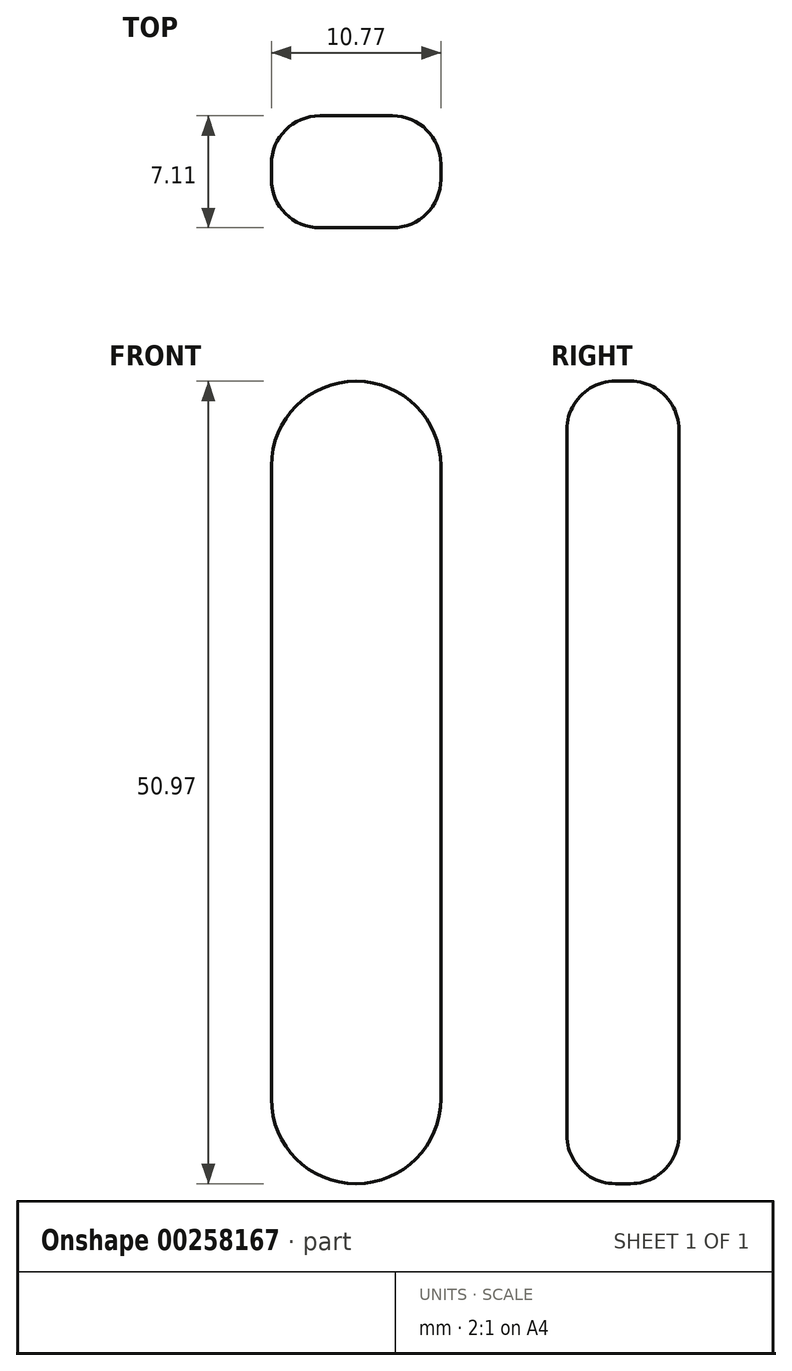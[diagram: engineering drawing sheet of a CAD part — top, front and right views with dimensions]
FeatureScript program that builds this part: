
annotation { "Feature Type Name" : "Feature", "Feature Type Description" : "" }
export const myFeature = defineFeature(function(context is Context, id is Id, definition is map)
    precondition{}
    {
        {
            var Q0;
            Q0=qCreatedBy(makeId("Front.planeOp"),FACE);
            var sketch = newSketch(context, id + "F0", { "sketchPlane" : qUnion([Q0])});
            skLineSegment(sketch, "E0", {"start": v(5.5, -31.28) * mm, "end": v(5.5, -5.4) * mm});
            skLineSegment(sketch, "E1", {"start": v(-5.26, -31.28) * mm, "end": v(-5.26, -12.39) * mm});
            skLineSegment(sketch, "E2", {"start": v(-5.26, -12.39) * mm, "end": v(-5.26, -5.4) * mm});
            skArc(sketch, "E3", {"start": v(-5.26, -5.4) * mm, "mid": v(0.12, -0.02) * mm, "end": v(5.5, -5.4) * mm});
            skArc(sketch, "E4", {"start": v(-5.26, -5.4) * mm, "mid": v(0.12, -10.79) * mm, "end": v(5.5, -5.4) * mm});
            skLineSegment(sketch, "E5", {"start": v(-5.26, -5.4) * mm, "end": v(5.5, -5.4) * mm});
            skLineSegment(sketch, "E6", {"start": v(-5.26, -5.4) * mm, "end": v(-5.26, 2.41) * mm});
            skLineSegment(sketch, "E7", {"start": v(-5.26, 2.41) * mm, "end": v(-5.26, 8.92) * mm});
            skLineSegment(sketch, "E8", {"start": v(5.5, -5.4) * mm, "end": v(5.5, 8.92) * mm});
            skLineSegment(sketch, "E9", {"start": v(5.5, 8.92) * mm, "end": v(5.5, 1.76) * mm});
            skLineSegment(sketch, "E10", {"start": v(5.5, 1.76) * mm, "end": v(5.5, 5.97) * mm});
            skArc(sketch, "E11", {"start": v(-5.26, 8.92) * mm, "mid": v(0.12, 14.3) * mm, "end": v(5.5, 8.92) * mm});
            skArc(sketch, "E12", {"start": v(5.5, -31.28) * mm, "mid": v(0.12, -36.67) * mm, "end": v(-5.26, -31.28) * mm});
            skSolve(sketch);
        }
        {
            var Q0;
            Q0=makeQuery(id+"F0.imprint","IMPRINT",FACE,{"disambiguationData":[TD([[makeQuery(id+"F0.imprint","IMPRINT",EDGE,{"derivedFrom":sQuery(id+"F0.wireOp",EDGE,"E3")}),1.0]])]});
            var Q1;
            Q1=makeQuery(id+"F0.imprint","IMPRINT",FACE,{"disambiguationData":[TD([[makeQuery(id+"F0.imprint","IMPRINT",EDGE,{"derivedFrom":sQuery(id+"F0.wireOp",EDGE,"E3")}),-1.0]])]});
            var Q2;
            Q2=makeQuery(id+"F0.imprint","IMPRINT",FACE,{"disambiguationData":[TD([[makeQuery(id+"F0.imprint","IMPRINT",EDGE,{"derivedFrom":sQuery(id+"F0.wireOp",EDGE,"E4")}),1.0]])]});
            var Q3;
            Q3=makeQuery(id+"F0.imprint","IMPRINT",FACE,{"disambiguationData":[TD([[makeQuery(id+"F0.imprint","IMPRINT",EDGE,{"derivedFrom":sQuery(id+"F0.wireOp",EDGE,"E0")}),1.0]])]});
            extrude(context, id + "F1", {"entities" : qUnion([Q0, Q1, Q2, Q3]), "depth" : 7.11 * mm});
        }
        {
            var Q0;
            Q0=makeQuery(id+"F1.opExtrude","CAP_EDGE",EDGE,{"disambiguationData":[OSD([sQuery(id+"F0.wireOp",EDGE,"E0"),sQuery(id+"F0.wireOp",EDGE,"E8"),sQuery(id+"F0.wireOp",EDGE,"E9"),sQuery(id+"F0.wireOp",EDGE,"E10")])],"isStart":false});
            var Q1;
            Q1=makeQuery(id+"F1.opExtrude","CAP_EDGE",EDGE,{"disambiguationData":[OSD([sQuery(id+"F0.wireOp",EDGE,"E0"),sQuery(id+"F0.wireOp",EDGE,"E8"),sQuery(id+"F0.wireOp",EDGE,"E9"),sQuery(id+"F0.wireOp",EDGE,"E10")])],"isStart":true});
            var Q2;
            Q2=makeQuery(id+"F1.opExtrude","CAP_EDGE",EDGE,{"disambiguationData":[OSD([sQuery(id+"F0.wireOp",EDGE,"E1"),sQuery(id+"F0.wireOp",EDGE,"E2"),sQuery(id+"F0.wireOp",EDGE,"E6"),sQuery(id+"F0.wireOp",EDGE,"E7")])],"isStart":true});
            var Q3;
            Q3=makeQuery(id+"F1.opExtrude","CAP_EDGE",EDGE,{"disambiguationData":[OSD([sQuery(id+"F0.wireOp",EDGE,"E1"),sQuery(id+"F0.wireOp",EDGE,"E2"),sQuery(id+"F0.wireOp",EDGE,"E6"),sQuery(id+"F0.wireOp",EDGE,"E7")])],"isStart":false});
            var Q4;
            Q4=makeQuery(id+"F1.opExtrude","CAP_EDGE",EDGE,{"disambiguationData":[OSD([sQuery(id+"F0.wireOp",EDGE,"E11")])],"isStart":true});
            var Q5;
            Q5=makeQuery(id+"F1.opExtrude","CAP_EDGE",EDGE,{"disambiguationData":[OSD([sQuery(id+"F0.wireOp",EDGE,"E11")])],"isStart":false});
            var Q6;
            Q6=makeQuery(id+"F1.opExtrude","CAP_EDGE",EDGE,{"disambiguationData":[OSD([sQuery(id+"F0.wireOp",EDGE,"E12")])],"isStart":true});
            var Q7;
            Q7=makeQuery(id+"F1.opExtrude","CAP_EDGE",EDGE,{"disambiguationData":[OSD([sQuery(id+"F0.wireOp",EDGE,"E12")])],"isStart":false});
            fillet(context, id + "F2", {"entities" : qUnion([Q0, Q1, Q2, Q3, Q4, Q5, Q6, Q7]), "radius" : 3.07 * mm, "tangentPropagation" : true, "allowEdgeOverflow" : false});
        }
    });
